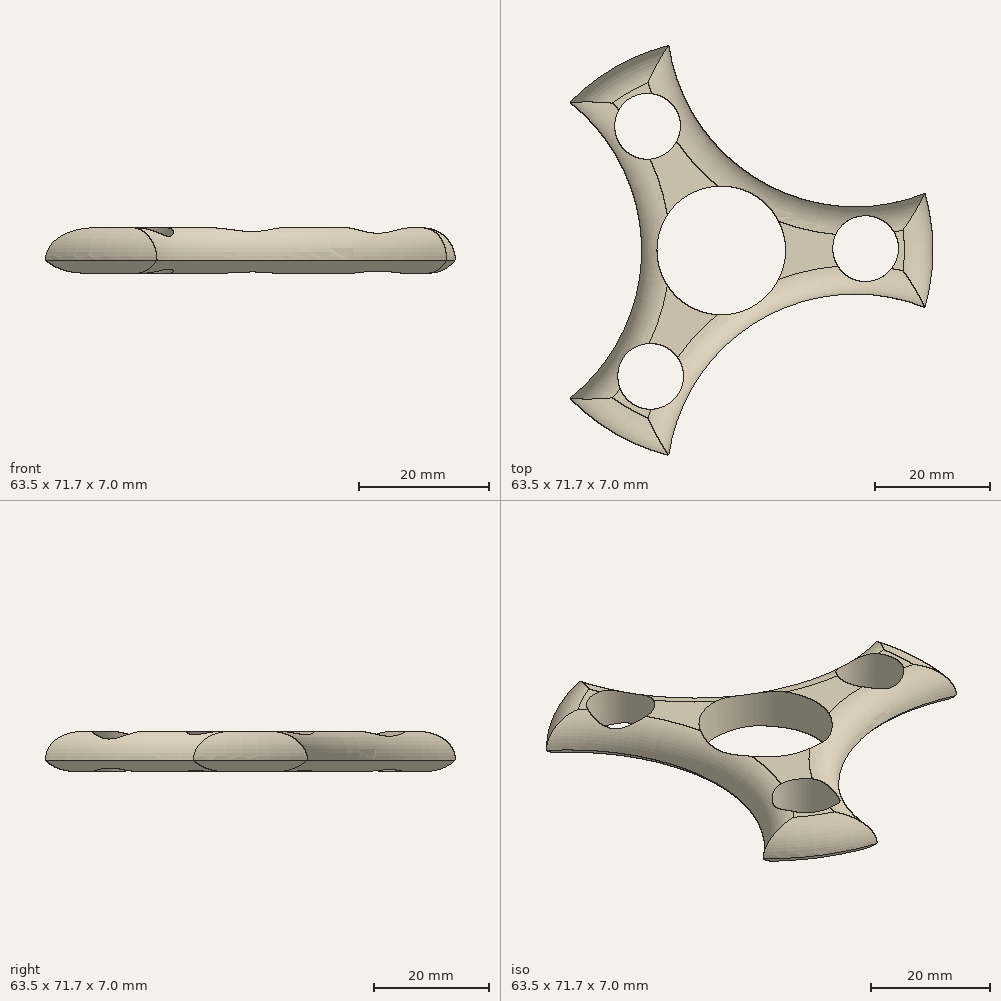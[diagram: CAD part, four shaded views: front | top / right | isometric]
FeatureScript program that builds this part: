
annotation { "Feature Type Name" : "Feature", "Feature Type Description" : "" }
export const myFeature = defineFeature(function(context is Context, id is Id, definition is map)
    precondition{}
    {
        {
            var Q0;
            Q0=qCreatedBy(makeId("Top.planeOp"),FACE);
            var sketch = newSketch(context, id + "F0", { "sketchPlane" : qUnion([Q0])});
            skCircle(sketch, "E0", {"center": v(0, 0) * mm, "radius": 11.25 * mm});
            skArc(sketch, "E1", {"start": v(-26.45, -25.88) * mm, "mid": v(-18.5, -32.04) * mm, "end": v(-9.19, -35.84) * mm});
            skArc(sketch, "E2", {"start": v(-26.45, -25.88) * mm, "mid": v(-13.92, 0) * mm, "end": v(-26.45, 25.88) * mm});
            skArc(sketch, "E3.1.0", {"start": v(35.63, -9.96) * mm, "mid": v(6.96, -12.06) * mm, "end": v(-9.19, -35.84) * mm});
            skArc(sketch, "E3.2.0", {"start": v(-9.19, 35.84) * mm, "mid": v(6.96, 12.06) * mm, "end": v(35.63, 9.96) * mm});
            skArc(sketch, "E4.trimOffspring", {"start": v(-9.19, 35.84) * mm, "mid": v(-18.5, 32.04) * mm, "end": v(-26.45, 25.88) * mm});
            skArc(sketch, "E5.trimOffspring", {"start": v(35.63, -9.96) * mm, "mid": v(37, 0) * mm, "end": v(35.63, 9.96) * mm});
            skCircle(sketch, "E6", {"center": v(-12.35, -22.02) * mm, "radius": 5.75 * mm});
            skCircle(sketch, "E7.1.0", {"center": v(25.24, 0.31) * mm, "radius": 5.75 * mm});
            skCircle(sketch, "E7.2.0", {"center": v(-12.9, 21.7) * mm, "radius": 5.75 * mm});
            skSolve(sketch);
        }
        {
            var Q0;
            Q0 = qSketchRegion(id + "F0", true);
            extrude(context, id + "F1", {"entities" : qUnion([Q0]), "depth" : 7 * mm, "offsetDistance" : 25 * mm});
        }
        {
            var Q0;
            Q0=makeQuery(id+"F1.opExtrude","CAP_EDGE",EDGE,{"disambiguationData":[OSD([sQuery(id+"F0.wireOp",EDGE,"E3.2.0")])],"isStart":false});
            var Q1;
            Q1=makeQuery(id+"F1.opExtrude","CAP_EDGE",EDGE,{"disambiguationData":[OSD([sQuery(id+"F0.wireOp",EDGE,"E3.1.0")])],"isStart":false});
            var Q2;
            Q2=makeQuery(id+"F1.opExtrude","CAP_EDGE",EDGE,{"disambiguationData":[OSD([sQuery(id+"F0.wireOp",EDGE,"E2")])],"isStart":false});
            var Q3;
            Q3=makeQuery(id+"F1.opExtrude","CAP_EDGE",EDGE,{"disambiguationData":[OSD([sQuery(id+"F0.wireOp",EDGE,"E4.trimOffspring")])],"isStart":false});
            var Q4;
            Q4=makeQuery(id+"F1.opExtrude","CAP_EDGE",EDGE,{"disambiguationData":[OSD([sQuery(id+"F0.wireOp",EDGE,"E5.trimOffspring")])],"isStart":false});
            var Q5;
            Q5=makeQuery(id+"F1.opExtrude","CAP_EDGE",EDGE,{"disambiguationData":[OSD([sQuery(id+"F0.wireOp",EDGE,"E1")])],"isStart":false});
            fillet(context, id + "F2", {"entities" : qUnion([Q0, Q1, Q2, Q3, Q4, Q5]), "radius" : 5 * mm, "tangentPropagation" : true, "allowEdgeOverflow" : false});
        }
        {
            var Q0;
            Q0=makeQuery(id+"F1.opExtrude","CAP_EDGE",EDGE,{"disambiguationData":[OSD([sQuery(id+"F0.wireOp",EDGE,"E1")])],"isStart":true});
            var Q1;
            Q1=makeQuery(id+"F1.opExtrude","CAP_EDGE",EDGE,{"disambiguationData":[OSD([sQuery(id+"F0.wireOp",EDGE,"E3.1.0")])],"isStart":true});
            var Q2;
            Q2=makeQuery(id+"F1.opExtrude","CAP_EDGE",EDGE,{"disambiguationData":[OSD([sQuery(id+"F0.wireOp",EDGE,"E5.trimOffspring")])],"isStart":true});
            var Q3;
            Q3=makeQuery(id+"F1.opExtrude","CAP_EDGE",EDGE,{"disambiguationData":[OSD([sQuery(id+"F0.wireOp",EDGE,"E3.2.0")])],"isStart":true});
            var Q4;
            Q4=makeQuery(id+"F1.opExtrude","CAP_EDGE",EDGE,{"disambiguationData":[OSD([sQuery(id+"F0.wireOp",EDGE,"E4.trimOffspring")])],"isStart":true});
            var Q5;
            Q5=makeQuery(id+"F1.opExtrude","CAP_EDGE",EDGE,{"disambiguationData":[OSD([sQuery(id+"F0.wireOp",EDGE,"E2")])],"isStart":true});
            fillet(context, id + "F3", {"entities" : qUnion([Q0, Q1, Q2, Q3, Q4, Q5]), "radius" : 5 * mm, "tangentPropagation" : true, "allowEdgeOverflow" : false});
        }
    });
